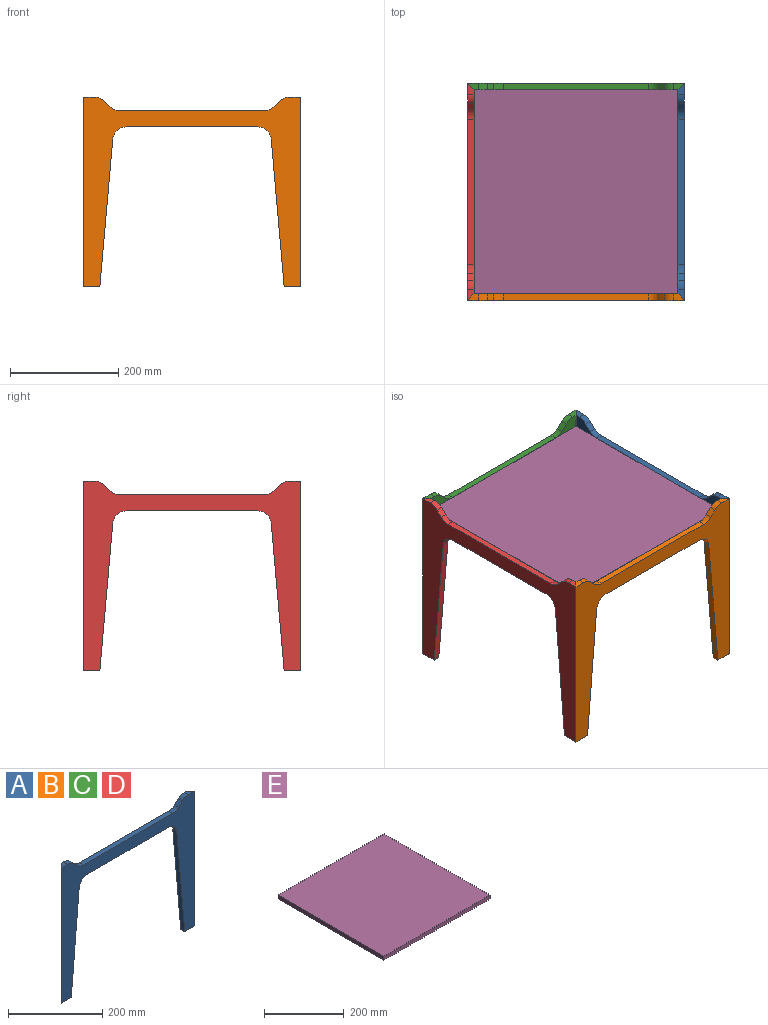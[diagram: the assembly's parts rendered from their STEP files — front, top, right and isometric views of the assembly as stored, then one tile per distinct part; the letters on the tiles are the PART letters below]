
ASSEMBLY  parts=5 mates=11
PART A: 20 faces, bbox 400x12x350 mm
  f0: plane 30x12mm, normal (0,0,-1), area 288mm2, adj f1,f10,f11,f12
  f1: plane 272.18x23.81mm, normal (1,0,-0.09), area 3278.6mm2, adj f0,f10,f11,f14
  f2: plane 242.57x12mm, normal (0,0,-1), area 2910.8mm2, adj f10,f11,f14,f15
  f3: plane 272.18x23.81mm, normal (-1,0,-0.09), area 3278.6mm2, adj f4,f10,f11,f15
  f4: plane 30x12mm, normal (0,0,-1), area 288mm2, adj f3,f10,f11,f13
  f5: plane 19.88x12mm, normal (0,0,1), area 166.5mm2, adj f10,f11,f13,f16
  f6: plane 12x11.27mm, normal (-0.7,0,0.72), area 188.2mm2, adj f10,f11,f16,f17
  f7: plane 268.14x12mm, normal (0,0,1), area 3217.6mm2, adj f10,f11,f17,f18
  f8: plane 12x11.27mm, normal (0.7,0,0.72), area 188.2mm2, adj f10,f11,f18,f19
  f9: plane 19.88x12mm, normal (0,0,1), area 166.5mm2, adj f10,f11,f12,f19
  f10: plane 400x350mm, normal (0,-1,0), area 39677.1mm2, adj f0,f1,f2,f3,f4,f5,f6,f7
  f11: plane 376x350mm, normal (0,1,0), area 31277.1mm2, adj f0,f1,f2,f3,f4,f5,f6,f7
  f12: plane 350x12mm, normal (-0.71,0.71,0), area 5939.7mm2, adj f0,f9,f10,f11
  f13: plane 350x12mm, normal (0.71,0.71,0), area 5939.7mm2, adj f4,f5,f10,f11
  f14: cylinder r=25mm len=24.91mm, axis (0,-1,0), area 445.1mm2, adj f1,f2,f10,f11
  f15: cylinder r=25mm len=24.91mm, axis (0,1,0), area 445.1mm2, adj f2,f3,f10,f11
  f16: cylinder r=25mm len=17.39mm, axis (0,1,0), area 230.8mm2, adj f5,f6,f10,f11
  f17: cylinder r=25mm len=17.39mm, axis (0,-1,0), area 230.8mm2, adj f6,f7,f10,f11
  f18: cylinder r=25mm len=17.39mm, axis (0,1,0), area 230.8mm2, adj f7,f8,f10,f11
  f19: cylinder r=25mm len=17.39mm, axis (0,1,0), area 230.8mm2, adj f8,f9,f10,f11
PART B: same geometry as A
PART C: same geometry as A
PART D: same geometry as A
PART E: 6 faces, bbox 376x376x12 mm
  f0: plane 376x12mm, normal (1,0,0), area 4512mm2, adj f1,f3,f4,f5
  f1: plane 376x12mm, normal (0,1,0), area 4512mm2, adj f0,f2,f4,f5
  f2: plane 376x12mm, normal (-1,0,0), area 4512mm2, adj f1,f3,f4,f5
  f3: plane 376x12mm, normal (0,-1,0), area 4512mm2, adj f0,f2,f4,f5
  f4: plane 376x376mm, normal (0,0,1), area 141376mm2, adj f0,f1,f2,f3
  f5: plane 376x376mm, normal (0,0,-1), area 141376mm2, adj f0,f1,f2,f3
PLACE A rot(axis=(0,0,1),90deg) t=(-101.13,-18.03,44.04)mm
PLACE B t=(-289.13,-206.03,44.04)mm fixed
PLACE C rot(axis=(0,0,-1),180deg) t=(-289.13,169.97,44.04)mm
PLACE D rot(axis=(0,0,-1),90deg) t=(-477.13,-18.03,44.04)mm
PLACE E t=(-289.13,-18.03,357.04)mm
MATE planar E.f4 <-> D.f7  axis (0,0,1) through (-289.13,-18.03,369.04)mm
MATE planar C.f9 <-> A.f5  axis (0,0,1) through (-101.64,176.84,394.04)mm
MATE planar C.f13 <-> D.f12  axis (-0.71,-0.71,0) through (-483.13,175.97,219.04)mm
MATE planar E.f3 <-> B.f11  axis (0,-1,0) through (-289.13,-206.03,363.04)mm
MATE planar B.f12 <-> D.f13  axis (-0.71,0.71,0) through (-483.13,-212.03,219.04)mm
MATE planar A.f13 <-> C.f12  axis (-0.71,0.71,0) through (-95.13,175.97,394.04)mm
MATE planar A.f12 <-> B.f13  axis (-0.71,-0.71,0) through (-95.13,-212.03,219.04)mm
MATE planar C.f12 <-> A.f13  axis (0.71,-0.71,0) through (-95.13,175.97,394.04)mm
MATE planar D.f9 <-> C.f5  axis (0,0,1) through (-484,169.46,394.04)mm
MATE planar A.f9 <-> B.f5  axis (0,0,1) through (-94.27,-205.52,394.04)mm
MATE planar D.f11 <-> E.f2  axis (1,0,0) through (-477.13,116.04,369.04)mm
